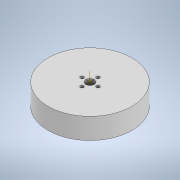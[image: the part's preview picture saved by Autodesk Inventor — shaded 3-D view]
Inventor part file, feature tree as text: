
AUTODESK INVENTOR PART (.ipt)
format: ipt  version: 2020 (Build 240168000, 168)  size: 113,664 bytes
history: native  units: in
note: dims shown in document units (in); Inventor stores cm internally (conversion verified against a paired STEP export)
features: sketch x3, extrude x2, other x1, pattern_circular x1
ambient origin geometry x8: Origin, YZ Plane, XZ Plane, XY Plane, X Axis, Y Axis, Z Axis, Center Point
bodies: Solid1 (feature_tree)
feature tree (7):
  extrude  "Extrusion1"  Depth=0.4in
  extrude  "Extrusion2"  Depth=1.0in
  sketch  "Sketch3"  dims[d5=0.16in d6=1.0in d7=0.0in d8=1.5748in d9=360.0deg]
  other  "Work Axis1"
  pattern_circular  "Circular Pattern1"  [2 undecoded]
  sketch  "Sketch1"  dims[d0=4.0in d1=0.4in]
  sketch  "Sketch2"  dims[d2=1.0in d3=0.0in d4=0.18in]
note: 2 required parameter values undecoded (feature->parameter linkage not recoverable at this tier; creation-order binding heuristic only, values carry confidence <= 0.55)
